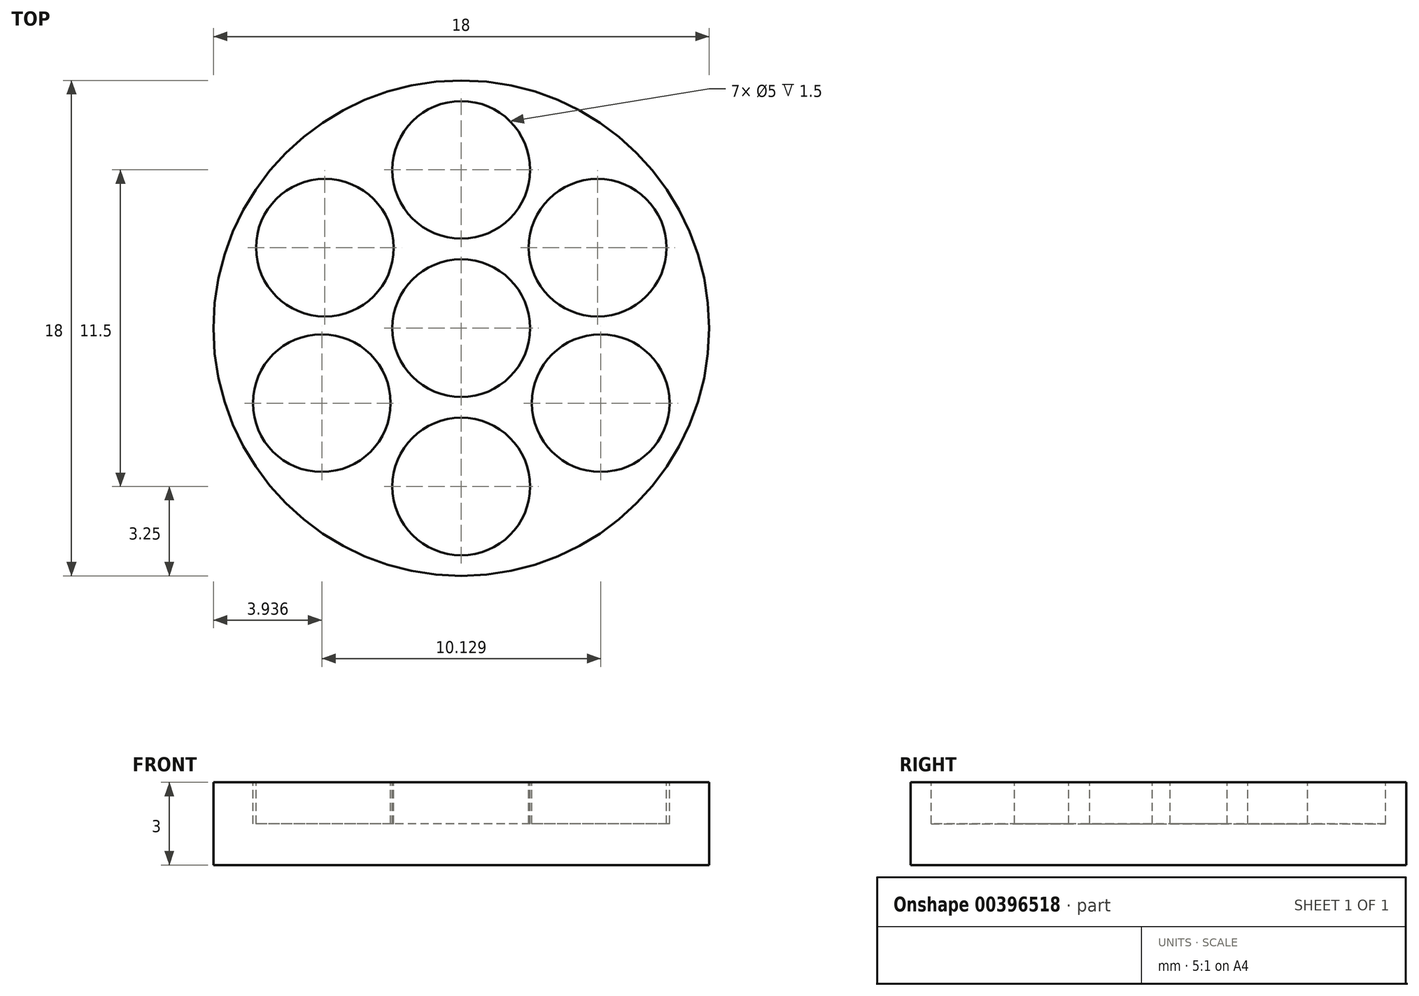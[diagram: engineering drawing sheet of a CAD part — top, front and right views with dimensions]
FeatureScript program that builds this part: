
annotation { "Feature Type Name" : "Feature", "Feature Type Description" : "" }
export const myFeature = defineFeature(function(context is Context, id is Id, definition is map)
    precondition{}
    {
        {
            var Q0;
            Q0=qCreatedBy(makeId("Top.planeOp"),FACE);
            var sketch = newSketch(context, id + "F0", { "sketchPlane" : qUnion([Q0])});
            skCircle(sketch, "E0", {"center": v(0, 0) * mm, "radius": 9 * mm});
            skCircle(sketch, "E1", {"center": v(0, 0) * mm, "radius": 3 * mm});
            skCircle(sketch, "E2", {"center": v(0, 6) * mm, "radius": 3 * mm});
            skCircle(sketch, "E3", {"center": v(0, -6) * mm, "radius": 3 * mm});
            skCircle(sketch, "E4", {"center": v(5.2, -3) * mm, "radius": 3 * mm});
            skCircle(sketch, "E5", {"center": v(5.2, 3) * mm, "radius": 3 * mm});
            skCircle(sketch, "E6", {"center": v(-5.2, 3) * mm, "radius": 3 * mm});
            skCircle(sketch, "E7", {"center": v(-5.2, -3) * mm, "radius": 3 * mm});
            skSolve(sketch);
        }
        {
            var Q0;
            {var subQ0=sQuery(id+"F0.wireOp",EDGE,"E4");var subQ1=makeQuery(id+"F0.imprint","INTERSECT",VERTEX,{"derivedFrom":[sQuery(id+"F0.wireOp",EDGE,"E1"),subQ0]});Q0=makeQuery(id+"F0.imprint","IMPRINT",FACE,{"disambiguationData":[TD([[makeQuery(id+"F0.imprint","IMPRINT",EDGE,{"disambiguationData":[TD([[subQ1,1.0]])],"derivedFrom":subQ0}),1.0]])]});}
            var Q1;
            {var subQ0=sQuery(id+"F0.wireOp",EDGE,"E6");var subQ1=makeQuery(id+"F0.imprint","INTERSECT",VERTEX,{"derivedFrom":[sQuery(id+"F0.wireOp",EDGE,"E0"),subQ0]});Q1=makeQuery(id+"F0.imprint","IMPRINT",FACE,{"disambiguationData":[TD([[makeQuery(id+"F0.imprint","IMPRINT",EDGE,{"disambiguationData":[TD([[subQ1,1.0]])],"derivedFrom":subQ0}),1.0]])]});}
            var Q2;
            {var subQ0=sQuery(id+"F0.wireOp",EDGE,"E2");var subQ1=sQuery(id+"F0.wireOp",EDGE,"E0");var subQ2=makeQuery(id+"F0.imprint","INTERSECT",VERTEX,{"derivedFrom":[subQ1,subQ0]});Q2=makeQuery(id+"F0.imprint","IMPRINT",FACE,{"disambiguationData":[TD([[makeQuery(id+"F0.imprint","IMPRINT",EDGE,{"disambiguationData":[TD([[subQ2,1.0]])],"derivedFrom":subQ1}),1.0]])]});}
            var Q3;
            {var subQ0=sQuery(id+"F0.wireOp",EDGE,"E2");var subQ1=sQuery(id+"F0.wireOp",EDGE,"E1");var subQ2=makeQuery(id+"F0.imprint","INTERSECT",VERTEX,{"derivedFrom":[subQ1,subQ0]});Q3=makeQuery(id+"F0.imprint","IMPRINT",FACE,{"disambiguationData":[TD([[makeQuery(id+"F0.imprint","IMPRINT",EDGE,{"disambiguationData":[TD([[subQ2,1.0]])],"derivedFrom":subQ1}),-1.0]])]});}
            var Q4;
            {var subQ0=sQuery(id+"F0.wireOp",EDGE,"E3");var subQ1=makeQuery(id+"F0.imprint","INTERSECT",VERTEX,{"derivedFrom":[sQuery(id+"F0.wireOp",EDGE,"E1"),subQ0]});Q4=makeQuery(id+"F0.imprint","IMPRINT",FACE,{"disambiguationData":[TD([[makeQuery(id+"F0.imprint","IMPRINT",EDGE,{"disambiguationData":[TD([[subQ1,1.0]])],"derivedFrom":subQ0}),1.0]])]});}
            var Q5;
            {var subQ0=sQuery(id+"F0.wireOp",EDGE,"E1");var subQ4=makeQuery(id+"F0.imprint","INTERSECT",VERTEX,{"derivedFrom":[subQ0,sQuery(id+"F0.wireOp",EDGE,"E2")]});Q5=makeQuery(id+"F0.imprint","IMPRINT",FACE,{"disambiguationData":[TD([[makeQuery(id+"F0.imprint","IMPRINT",EDGE,{"disambiguationData":[TD([[subQ4,1.0]])],"derivedFrom":subQ0}),1.0]])]});}
            var Q6;
            {var subQ0=sQuery(id+"F0.wireOp",EDGE,"E5");var subQ1=makeQuery(id+"F0.imprint","INTERSECT",VERTEX,{"derivedFrom":[sQuery(id+"F0.wireOp",EDGE,"E0"),subQ0]});Q6=makeQuery(id+"F0.imprint","IMPRINT",FACE,{"disambiguationData":[TD([[makeQuery(id+"F0.imprint","IMPRINT",EDGE,{"disambiguationData":[TD([[subQ1,-1.0]])],"derivedFrom":subQ0}),1.0]])]});}
            var Q7;
            {var subQ0=sQuery(id+"F0.wireOp",EDGE,"E2");var subQ1=sQuery(id+"F0.wireOp",EDGE,"E0");var subQ2=makeQuery(id+"F0.imprint","INTERSECT",VERTEX,{"derivedFrom":[subQ1,subQ0]});Q7=makeQuery(id+"F0.imprint","IMPRINT",FACE,{"disambiguationData":[TD([[makeQuery(id+"F0.imprint","IMPRINT",EDGE,{"disambiguationData":[TD([[subQ2,-1.0]])],"derivedFrom":subQ1}),1.0]])]});}
            var Q8;
            {var subQ0=sQuery(id+"F0.wireOp",EDGE,"E6");var subQ1=sQuery(id+"F0.wireOp",EDGE,"E0");var subQ2=makeQuery(id+"F0.imprint","INTERSECT",VERTEX,{"derivedFrom":[subQ1,subQ0]});Q8=makeQuery(id+"F0.imprint","IMPRINT",FACE,{"disambiguationData":[TD([[makeQuery(id+"F0.imprint","IMPRINT",EDGE,{"disambiguationData":[TD([[subQ2,-1.0]])],"derivedFrom":subQ1}),1.0]])]});}
            var Q9;
            {var subQ0=sQuery(id+"F0.wireOp",EDGE,"E7");var subQ1=sQuery(id+"F0.wireOp",EDGE,"E0");var subQ2=makeQuery(id+"F0.imprint","INTERSECT",VERTEX,{"derivedFrom":[subQ1,subQ0]});Q9=makeQuery(id+"F0.imprint","IMPRINT",FACE,{"disambiguationData":[TD([[makeQuery(id+"F0.imprint","IMPRINT",EDGE,{"disambiguationData":[TD([[subQ2,-1.0]])],"derivedFrom":subQ1}),1.0]])]});}
            var Q10;
            {var subQ0=sQuery(id+"F0.wireOp",EDGE,"E7");var subQ1=makeQuery(id+"F0.imprint","INTERSECT",VERTEX,{"derivedFrom":[sQuery(id+"F0.wireOp",EDGE,"E1"),subQ0]});Q10=makeQuery(id+"F0.imprint","IMPRINT",FACE,{"disambiguationData":[TD([[makeQuery(id+"F0.imprint","IMPRINT",EDGE,{"disambiguationData":[TD([[subQ1,-1.0]])],"derivedFrom":subQ0}),1.0]])]});}
            var Q11;
            {var subQ0=sQuery(id+"F0.wireOp",EDGE,"E3");var subQ1=sQuery(id+"F0.wireOp",EDGE,"E0");var subQ2=makeQuery(id+"F0.imprint","INTERSECT",VERTEX,{"derivedFrom":[subQ1,subQ0]});Q11=makeQuery(id+"F0.imprint","IMPRINT",FACE,{"disambiguationData":[TD([[makeQuery(id+"F0.imprint","IMPRINT",EDGE,{"disambiguationData":[TD([[subQ2,-1.0]])],"derivedFrom":subQ1}),1.0]])]});}
            var Q12;
            {var subQ0=sQuery(id+"F0.wireOp",EDGE,"E5");var subQ1=sQuery(id+"F0.wireOp",EDGE,"E0");var subQ2=makeQuery(id+"F0.imprint","INTERSECT",VERTEX,{"derivedFrom":[subQ1,subQ0]});Q12=makeQuery(id+"F0.imprint","IMPRINT",FACE,{"disambiguationData":[TD([[makeQuery(id+"F0.imprint","IMPRINT",EDGE,{"disambiguationData":[TD([[subQ2,1.0]])],"derivedFrom":subQ1}),1.0]])]});}
            var Q13;
            {var subQ0=sQuery(id+"F0.wireOp",EDGE,"E2");var subQ1=sQuery(id+"F0.wireOp",EDGE,"E1");var subQ2=makeQuery(id+"F0.imprint","INTERSECT",VERTEX,{"derivedFrom":[subQ1,subQ0]});Q13=makeQuery(id+"F0.imprint","IMPRINT",FACE,{"disambiguationData":[TD([[makeQuery(id+"F0.imprint","IMPRINT",EDGE,{"disambiguationData":[TD([[subQ2,-1.0]])],"derivedFrom":subQ1}),-1.0]])]});}
            var Q14;
            {var subQ0=sQuery(id+"F0.wireOp",EDGE,"E6");var subQ1=sQuery(id+"F0.wireOp",EDGE,"E1");var subQ2=makeQuery(id+"F0.imprint","INTERSECT",VERTEX,{"derivedFrom":[subQ1,subQ0]});Q14=makeQuery(id+"F0.imprint","IMPRINT",FACE,{"disambiguationData":[TD([[makeQuery(id+"F0.imprint","IMPRINT",EDGE,{"disambiguationData":[TD([[subQ2,-1.0]])],"derivedFrom":subQ1}),-1.0]])]});}
            var Q15;
            {var subQ0=sQuery(id+"F0.wireOp",EDGE,"E7");var subQ1=sQuery(id+"F0.wireOp",EDGE,"E1");var subQ2=makeQuery(id+"F0.imprint","INTERSECT",VERTEX,{"derivedFrom":[subQ1,subQ0]});Q15=makeQuery(id+"F0.imprint","IMPRINT",FACE,{"disambiguationData":[TD([[makeQuery(id+"F0.imprint","IMPRINT",EDGE,{"disambiguationData":[TD([[subQ2,-1.0]])],"derivedFrom":subQ1}),-1.0]])]});}
            var Q16;
            {var subQ0=sQuery(id+"F0.wireOp",EDGE,"E3");var subQ1=sQuery(id+"F0.wireOp",EDGE,"E1");var subQ2=makeQuery(id+"F0.imprint","INTERSECT",VERTEX,{"derivedFrom":[subQ1,subQ0]});Q16=makeQuery(id+"F0.imprint","IMPRINT",FACE,{"disambiguationData":[TD([[makeQuery(id+"F0.imprint","IMPRINT",EDGE,{"disambiguationData":[TD([[subQ2,-1.0]])],"derivedFrom":subQ1}),-1.0]])]});}
            var Q17;
            {var subQ0=sQuery(id+"F0.wireOp",EDGE,"E5");var subQ1=sQuery(id+"F0.wireOp",EDGE,"E1");var subQ2=makeQuery(id+"F0.imprint","INTERSECT",VERTEX,{"derivedFrom":[subQ1,subQ0]});Q17=makeQuery(id+"F0.imprint","IMPRINT",FACE,{"disambiguationData":[TD([[makeQuery(id+"F0.imprint","IMPRINT",EDGE,{"disambiguationData":[TD([[subQ2,1.0]])],"derivedFrom":subQ1}),-1.0]])]});}
            var Q18;
            {var subQ0=sQuery(id+"F0.wireOp",EDGE,"E2");var subQ1=makeQuery(id+"F0.imprint","INTERSECT",VERTEX,{"derivedFrom":[sQuery(id+"F0.wireOp",EDGE,"E0"),subQ0]});Q18=makeQuery(id+"F0.imprint","IMPRINT",FACE,{"disambiguationData":[TD([[makeQuery(id+"F0.imprint","IMPRINT",EDGE,{"disambiguationData":[TD([[subQ1,-1.0]])],"derivedFrom":subQ0}),1.0]])]});}
            extrude(context, id + "F1", {"entities" : qUnion([Q0, Q1, Q2, Q3, Q4, Q5, Q6, Q7, Q8, Q9, Q10, Q11, Q12, Q13, Q14, Q15, Q16, Q17, Q18]), "depth" : 3 * mm});
        }
        {
            var Q0;
            Q0=makeQuery(id+"F1.opExtrude","CAP_FACE",FACE,{"disambiguationData":[OSD([sQuery(id+"F0.wireOp",EDGE,"E0")])],"isStart":false});
            var sketch = newSketch(context, id + "F2", { "sketchPlane" : qUnion([Q0])});
            skCircle(sketch, "E8", {"center": v(0, 0) * mm, "radius": 2.5 * mm});
            skCircle(sketch, "E9", {"center": v(0, 5.75) * mm, "radius": 2.5 * mm});
            skCircle(sketch, "E10", {"center": v(0, -5.75) * mm, "radius": 2.5 * mm});
            skCircle(sketch, "E11", {"center": v(4.95, 2.92) * mm, "radius": 2.5 * mm});
            skCircle(sketch, "E12", {"center": v(5.06, -2.72) * mm, "radius": 2.5 * mm});
            skCircle(sketch, "E13", {"center": v(-5.06, -2.72) * mm, "radius": 2.5 * mm});
            skCircle(sketch, "E14", {"center": v(-4.95, 2.92) * mm, "radius": 2.5 * mm});
            skSolve(sketch);
        }
        {
            var Q0;
            Q0=makeQuery(id+"F2.imprint","IMPRINT",FACE,{"disambiguationData":[TD([[makeQuery(id+"F2.imprint","IMPRINT",EDGE,{"derivedFrom":sQuery(id+"F2.wireOp",EDGE,"E9")}),1.0]])]});
            var Q1;
            Q1=makeQuery(id+"F2.imprint","IMPRINT",FACE,{"disambiguationData":[TD([[makeQuery(id+"F2.imprint","IMPRINT",EDGE,{"derivedFrom":sQuery(id+"F2.wireOp",EDGE,"E14")}),1.0]])]});
            var Q2;
            Q2=makeQuery(id+"F2.imprint","IMPRINT",FACE,{"disambiguationData":[TD([[makeQuery(id+"F2.imprint","IMPRINT",EDGE,{"derivedFrom":sQuery(id+"F2.wireOp",EDGE,"E8")}),1.0]])]});
            var Q3;
            Q3=makeQuery(id+"F2.imprint","IMPRINT",FACE,{"disambiguationData":[TD([[makeQuery(id+"F2.imprint","IMPRINT",EDGE,{"derivedFrom":sQuery(id+"F2.wireOp",EDGE,"E13")}),1.0]])]});
            var Q4;
            Q4=makeQuery(id+"F2.imprint","IMPRINT",FACE,{"disambiguationData":[TD([[makeQuery(id+"F2.imprint","IMPRINT",EDGE,{"derivedFrom":sQuery(id+"F2.wireOp",EDGE,"E10")}),1.0]])]});
            var Q5;
            Q5=makeQuery(id+"F2.imprint","IMPRINT",FACE,{"disambiguationData":[TD([[makeQuery(id+"F2.imprint","IMPRINT",EDGE,{"derivedFrom":sQuery(id+"F2.wireOp",EDGE,"E12")}),1.0]])]});
            var Q6;
            Q6=makeQuery(id+"F2.imprint","IMPRINT",FACE,{"disambiguationData":[TD([[makeQuery(id+"F2.imprint","IMPRINT",EDGE,{"derivedFrom":sQuery(id+"F2.wireOp",EDGE,"E11")}),1.0]])]});
            extrude(context, id + "F3", {"entities" : qUnion([Q0, Q1, Q2, Q3, Q4, Q5, Q6]), "operationType" : NewBodyOperationType.REMOVE, "oppositeDirection" : true, "depth" : 1.5 * mm});
        }
    });
